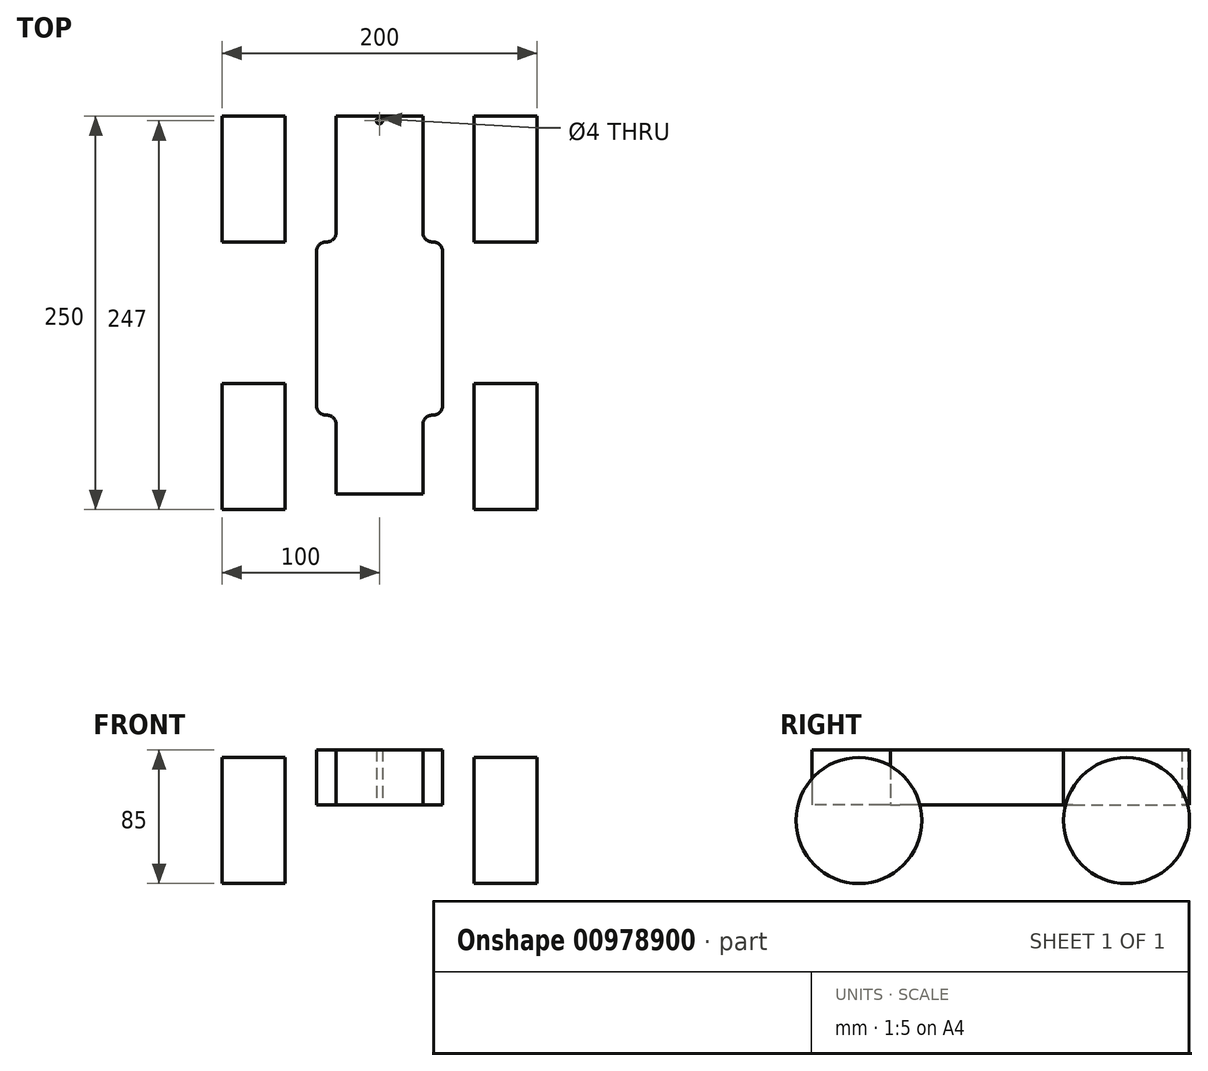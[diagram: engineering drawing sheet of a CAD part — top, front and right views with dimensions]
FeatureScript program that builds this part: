
annotation { "Feature Type Name" : "Feature", "Feature Type Description" : "" }
export const myFeature = defineFeature(function(context is Context, id is Id, definition is map)
    precondition{}
    {
        {
            var Q0;
            Q0=qCreatedBy(makeId("Top.planeOp"),FACE);
            var sketch = newSketch(context, id + "F0", { "sketchPlane" : qUnion([Q0])});
            skLineSegment(sketch, "E0.bottom", {"start": v(40, 55) * mm, "end": v(-40, 55) * mm});
            skLineSegment(sketch, "E0.top", {"start": v(40, -55) * mm, "end": v(-40, -55) * mm});
            skLineSegment(sketch, "E0.left", {"start": v(40, 55) * mm, "end": v(40, -55) * mm});
            skLineSegment(sketch, "E0.right", {"start": v(-40, 55) * mm, "end": v(-40, -55) * mm});
            skPoint(sketch, "E0.middle", {"position": v(0, 0) * mm});
            skLineSegment(sketch, "E1", {"start": v(0, 0) * mm, "end": v(0, 95) * mm, "construction": true});
            skLineSegment(sketch, "E2.bottom", {"start": v(27.5, 55) * mm, "end": v(-27.5, 55) * mm});
            skLineSegment(sketch, "E2.top", {"start": v(27.5, 135) * mm, "end": v(-27.5, 135) * mm});
            skLineSegment(sketch, "E2.left", {"start": v(27.5, 55) * mm, "end": v(27.5, 135) * mm});
            skLineSegment(sketch, "E2.right", {"start": v(-27.5, 55) * mm, "end": v(-27.5, 135) * mm});
            skPoint(sketch, "E2.middle", {"position": v(0, 95) * mm});
            skLineSegment(sketch, "E3", {"start": v(0, 0) * mm, "end": v(0, -80) * mm, "construction": true});
            skPoint(sketch, "E3.endSnap0", {"position": v(0, -55) * mm});
            skLineSegment(sketch, "E4.bottom", {"start": v(27.5, -55) * mm, "end": v(-27.5, -55) * mm});
            skLineSegment(sketch, "E4.top", {"start": v(27.5, -105) * mm, "end": v(-27.5, -105) * mm});
            skLineSegment(sketch, "E4.left", {"start": v(27.5, -55) * mm, "end": v(27.5, -105) * mm});
            skLineSegment(sketch, "E4.right", {"start": v(-27.5, -55) * mm, "end": v(-27.5, -105) * mm});
            skPoint(sketch, "E4.middle", {"position": v(0, -80) * mm});
            skLineSegment(sketch, "E5.bottom", {"start": v(27.5, -105) * mm, "end": v(34.5, -105) * mm});
            skLineSegment(sketch, "E5.top", {"start": v(27.5, -98) * mm, "end": v(34.5, -98) * mm});
            skLineSegment(sketch, "E5.left", {"start": v(27.5, -105) * mm, "end": v(27.5, -98) * mm});
            skLineSegment(sketch, "E5.right", {"start": v(34.5, -105) * mm, "end": v(34.5, -98) * mm});
            skLineSegment(sketch, "E6", {"start": v(34.5, -98) * mm, "end": v(27.5, -105) * mm, "construction": true});
            skPoint(sketch, "E7", {"position": v(31, -101.5) * mm});
            skCircle(sketch, "E8", {"center": v(31, -101.5) * mm, "radius": 2 * mm});
            skCircle(sketch, "E9.MirrorC", {"center": v(-31, -101.5) * mm, "radius": 2 * mm});
            skLineSegment(sketch, "E10.MirrorCS", {"start": v(-27.5, -98) * mm, "end": v(-34.5, -98) * mm});
            skLineSegment(sketch, "E11.MirrorCS", {"start": v(-34.5, -105) * mm, "end": v(-34.5, -98) * mm});
            skLineSegment(sketch, "E12.MirrorCS", {"start": v(-27.5, -105) * mm, "end": v(-34.5, -105) * mm});
            skPoint(sketch, "E13", {"position": v(0, 135) * mm});
            skLineSegment(sketch, "E14", {"start": v(0, 135) * mm, "end": v(0, 132) * mm, "construction": true});
            skCircle(sketch, "E15", {"center": v(0, 132) * mm, "radius": 2 * mm});
            skSolve(sketch);
        }
        {
            var Q0;
            Q0=makeQuery(id+"F0.imprint","IMPRINT",FACE,{"disambiguationData":[TD([[makeQuery(id+"F0.imprint","IMPRINT",EDGE,{"derivedFrom":sQuery(id+"F0.wireOp",EDGE,"E2.top")}),1.0]])]});
            var Q1;
            {var subQ5=sQuery(id+"F0.wireOp",EDGE,"E0.left");Q1=makeQuery(id+"F0.imprint","IMPRINT",FACE,{"disambiguationData":[TD([[makeQuery(id+"F0.imprint","IMPRINT",EDGE,{"derivedFrom":subQ5}),-1.0]])]});}
            var Q2;
            {var subQ4=sQuery(id+"F0.wireOp",EDGE,"E4.top");Q2=makeQuery(id+"F0.imprint","IMPRINT",FACE,{"disambiguationData":[TD([[makeQuery(id+"F0.imprint","IMPRINT",EDGE,{"derivedFrom":subQ4}),-1.0]])]});}
            extrude(context, id + "F1", {"entities" : qUnion([Q0, Q1, Q2]), "depth" : 35 * mm, "offsetDistance" : 25 * mm});
        }
        {
            var Q0;
            Q0=makeQuery(id+"F1.opExtrude","SWEPT_EDGE",EDGE,{"disambiguationData":[OSD([sQuery(id+"F0.wireOp",EDGE,"E0.top"),sQuery(id+"F0.wireOp",EDGE,"E4.left")])]});
            var Q1;
            Q1=makeQuery(id+"F1.opExtrude","SWEPT_EDGE",EDGE,{"disambiguationData":[OSD([sQuery(id+"F0.wireOp",EDGE,"E0.top"),sQuery(id+"F0.wireOp",EDGE,"E0.left")])]});
            var Q2;
            Q2=makeQuery(id+"F1.opExtrude","SWEPT_EDGE",EDGE,{"disambiguationData":[OSD([sQuery(id+"F0.wireOp",EDGE,"E0.top"),sQuery(id+"F0.wireOp",EDGE,"E0.right")])]});
            var Q3;
            Q3=makeQuery(id+"F1.opExtrude","SWEPT_EDGE",EDGE,{"disambiguationData":[OSD([sQuery(id+"F0.wireOp",EDGE,"E0.top"),sQuery(id+"F0.wireOp",EDGE,"E4.right")])]});
            var Q4;
            Q4=makeQuery(id+"F1.opExtrude","SWEPT_EDGE",EDGE,{"disambiguationData":[OSD([sQuery(id+"F0.wireOp",EDGE,"E0.bottom"),sQuery(id+"F0.wireOp",EDGE,"E0.right")])]});
            var Q5;
            Q5=makeQuery(id+"F1.opExtrude","SWEPT_EDGE",EDGE,{"disambiguationData":[OSD([sQuery(id+"F0.wireOp",EDGE,"E0.bottom"),sQuery(id+"F0.wireOp",EDGE,"E2.right")])]});
            var Q6;
            Q6=makeQuery(id+"F1.opExtrude","SWEPT_EDGE",EDGE,{"disambiguationData":[OSD([sQuery(id+"F0.wireOp",EDGE,"E0.bottom"),sQuery(id+"F0.wireOp",EDGE,"E0.left")])]});
            var Q7;
            Q7=makeQuery(id+"F1.opExtrude","SWEPT_EDGE",EDGE,{"disambiguationData":[OSD([sQuery(id+"F0.wireOp",EDGE,"E0.bottom"),sQuery(id+"F0.wireOp",EDGE,"E2.left")])]});
            fillet(context, id + "F2", {"entities" : qUnion([Q0, Q1, Q2, Q3, Q4, Q5, Q6, Q7]), "radius" : 6 * mm, "tangentPropagation" : true, "allowEdgeOverflow" : false});
        }
        {
            var Q0;
            Q0=qCreatedBy(makeId("Right.planeOp"),FACE);
            var sketch = newSketch(context, id + "F3", { "sketchPlane" : qUnion([Q0])});
            skCircle(sketch, "E16", {"center": v(-75, -10) * mm, "radius": 40 * mm});
            skCircle(sketch, "E17.1.0.0", {"center": v(95, -10) * mm, "radius": 40 * mm});
            skLineSegment(sketch, "E17.direction1", {"start": v(-75, -10) * mm, "end": v(95, -10) * mm, "construction": true});
            skSolve(sketch);
        }
        {
            var Q0;
            Q0=makeQuery(id+"F3.imprint","IMPRINT",FACE,{"disambiguationData":[TD([[makeQuery(id+"F3.imprint","IMPRINT",EDGE,{"derivedFrom":sQuery(id+"F3.wireOp",EDGE,"E16")}),1.0]])]});
            var Q1;
            Q1=makeQuery(id+"F3.imprint","IMPRINT",FACE,{"disambiguationData":[TD([[makeQuery(id+"F3.imprint","IMPRINT",EDGE,{"derivedFrom":sQuery(id+"F3.wireOp",EDGE,"E17.1.0.0")}),1.0]])]});
            extrude(context, id + "F4", {"entities" : qUnion([Q0, Q1]), "depth" : 100 * mm, "offsetDistance" : 25 * mm, "hasSecondDirection" : true, "secondDirectionOppositeDirection" : false, "secondDirectionDepth" : 60 * mm});
        }
        {
            var Q0;
            Q0=makeQuery(id+"F4.opExtrude","SWEPT_BODY",BODY,{"disambiguationData":[OSD([sQuery(id+"F3.wireOp",EDGE,"E16")])]});
            var Q1;
            Q1=makeQuery(id+"F4.opExtrude","SWEPT_BODY",BODY,{"disambiguationData":[OSD([sQuery(id+"F3.wireOp",EDGE,"E17.1.0.0")])]});
            var Q2;
            Q2=qCreatedBy(makeId("Right.planeOp"),FACE);
            mirror(context, id + "F5", {"entities" : qUnion([Q0, Q1]), "mirrorPlane" : qUnion([Q2])});
        }
    });
